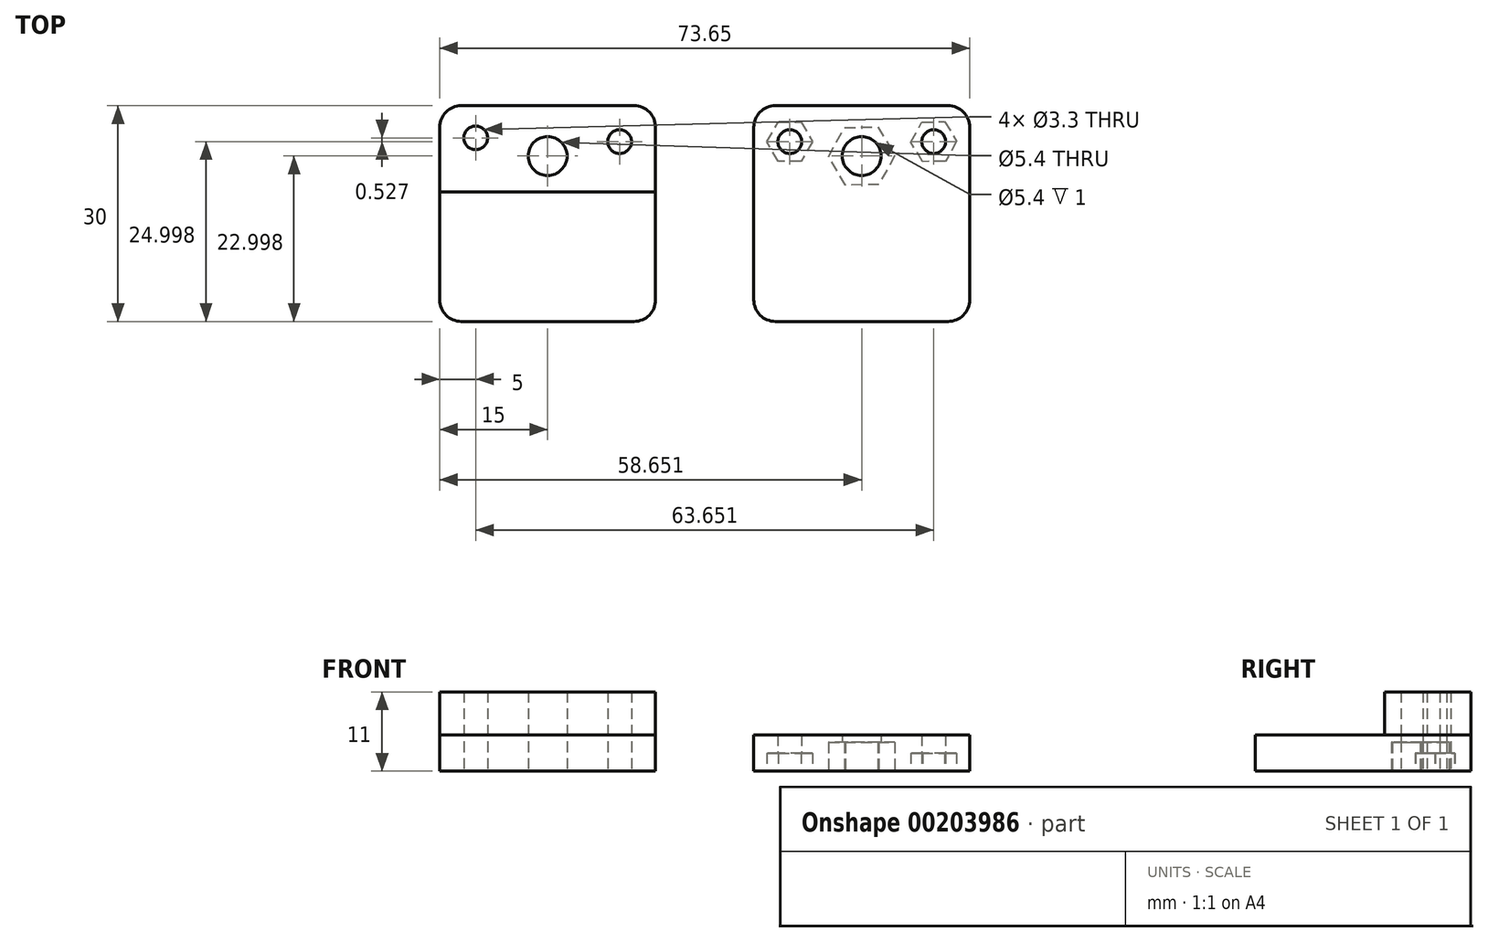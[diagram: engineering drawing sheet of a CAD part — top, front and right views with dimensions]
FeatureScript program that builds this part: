
annotation { "Feature Type Name" : "Feature", "Feature Type Description" : "" }
export const myFeature = defineFeature(function(context is Context, id is Id, definition is map)
    precondition{}
    {
        {
            var Q0;
            Q0=qCreatedBy(makeId("Top.planeOp"),FACE);
            var sketch = newSketch(context, id + "F0", { "sketchPlane" : qUnion([Q0])});
            skLineSegment(sketch, "E0.bottom", {"start": v(-35.25, 15.2) * mm, "end": v(-5.25, 15.2) * mm});
            skLineSegment(sketch, "E0.top", {"start": v(-35.25, -14.8) * mm, "end": v(-5.25, -14.8) * mm});
            skLineSegment(sketch, "E0.left", {"start": v(-35.25, 15.2) * mm, "end": v(-35.25, -14.8) * mm});
            skLineSegment(sketch, "E0.right", {"start": v(-5.25, 15.2) * mm, "end": v(-5.25, -14.8) * mm});
            skLineSegment(sketch, "E1.bottom", {"start": v(8.4, 15.2) * mm, "end": v(38.4, 15.2) * mm});
            skLineSegment(sketch, "E1.top", {"start": v(8.4, -14.8) * mm, "end": v(38.4, -14.8) * mm});
            skLineSegment(sketch, "E1.left", {"start": v(8.4, 15.2) * mm, "end": v(8.4, -14.8) * mm});
            skLineSegment(sketch, "E1.right", {"start": v(38.4, 15.2) * mm, "end": v(38.4, -14.8) * mm});
            skSolve(sketch);
        }
        {
            var Q0;
            Q0=makeQuery(id+"F0.imprint","IMPRINT",FACE,{"disambiguationData":[TD([[makeQuery(id+"F0.imprint","IMPRINT",EDGE,{"derivedFrom":sQuery(id+"F0.wireOp",EDGE,"E0.bottom")}),-1.0]])]});
            var Q1;
            Q1=makeQuery(id+"F0.imprint","IMPRINT",FACE,{"disambiguationData":[TD([[makeQuery(id+"F0.imprint","IMPRINT",EDGE,{"derivedFrom":sQuery(id+"F0.wireOp",EDGE,"E1.bottom")}),-1.0]])]});
            extrude(context, id + "F1", {"entities" : qUnion([Q0, Q1]), "depth" : 5 * mm});
        }
        {
            var Q0;
            Q0=makeQuery(id+"F1.opExtrude","CAP_FACE",FACE,{"disambiguationData":[OSD([sQuery(id+"F0.wireOp",EDGE,"E0.bottom"),sQuery(id+"F0.wireOp",EDGE,"E0.top"),sQuery(id+"F0.wireOp",EDGE,"E0.left"),sQuery(id+"F0.wireOp",EDGE,"E0.right")])],"isStart":false});
            var sketch = newSketch(context, id + "F2", { "sketchPlane" : qUnion([Q0])});
            skLineSegment(sketch, "E2.bottom", {"start": v(-35.25, 15.2) * mm, "end": v(-5.25, 15.2) * mm});
            skLineSegment(sketch, "E2.top", {"start": v(-35.25, 3.2) * mm, "end": v(-5.25, 3.2) * mm});
            skLineSegment(sketch, "E2.left", {"start": v(-35.25, 15.2) * mm, "end": v(-35.25, 3.2) * mm});
            skLineSegment(sketch, "E2.right", {"start": v(-5.25, 15.2) * mm, "end": v(-5.25, 3.2) * mm});
            skSolve(sketch);
        }
        {
            var Q0;
            Q0=makeQuery(id+"F2.imprint","IMPRINT",FACE,{"disambiguationData":[TD([[makeQuery(id+"F2.imprint","IMPRINT",EDGE,{"derivedFrom":sQuery(id+"F2.wireOp",EDGE,"E2.bottom")}),-1.0]])]});
            extrude(context, id + "F3", {"entities" : qUnion([Q0]), "operationType" : NewBodyOperationType.ADD, "depth" : 6 * mm});
        }
        {
            var Q0;
            Q0=qCreatedBy(makeId("Top.planeOp"),FACE);
            var sketch = newSketch(context, id + "F4", { "sketchPlane" : qUnion([Q0])});
            skCircle(sketch, "E3", {"center": v(23.4, 8.2) * mm, "radius": 2.7 * mm});
            skCircle(sketch, "E4", {"center": v(-20.25, 8.2) * mm, "radius": 2.7 * mm});
            skCircle(sketch, "E5", {"center": v(-30.25, 10.72) * mm, "radius": 1.65 * mm});
            skCircle(sketch, "E6", {"center": v(-10.25, 10.2) * mm, "radius": 1.65 * mm});
            skCircle(sketch, "E7", {"center": v(13.4, 10.2) * mm, "radius": 1.65 * mm});
            skCircle(sketch, "E8", {"center": v(33.4, 10.2) * mm, "radius": 1.65 * mm});
            skSolve(sketch);
        }
        {
            var Q0;
            Q0=makeQuery(id+"F4.imprint","IMPRINT",FACE,{"disambiguationData":[TD([[makeQuery(id+"F4.imprint","IMPRINT",EDGE,{"derivedFrom":sQuery(id+"F4.wireOp",EDGE,"E8")}),1.0]])]});
            var Q1;
            Q1=makeQuery(id+"F4.imprint","IMPRINT",FACE,{"disambiguationData":[TD([[makeQuery(id+"F4.imprint","IMPRINT",EDGE,{"derivedFrom":sQuery(id+"F4.wireOp",EDGE,"E3")}),1.0]])]});
            var Q2;
            Q2=makeQuery(id+"F4.imprint","IMPRINT",FACE,{"disambiguationData":[TD([[makeQuery(id+"F4.imprint","IMPRINT",EDGE,{"derivedFrom":sQuery(id+"F4.wireOp",EDGE,"E7")}),1.0]])]});
            var Q3;
            Q3=makeQuery(id+"F4.imprint","IMPRINT",FACE,{"disambiguationData":[TD([[makeQuery(id+"F4.imprint","IMPRINT",EDGE,{"derivedFrom":sQuery(id+"F4.wireOp",EDGE,"E6")}),1.0]])]});
            var Q4;
            Q4=makeQuery(id+"F4.imprint","IMPRINT",FACE,{"disambiguationData":[TD([[makeQuery(id+"F4.imprint","IMPRINT",EDGE,{"derivedFrom":sQuery(id+"F4.wireOp",EDGE,"E4")}),1.0]])]});
            var Q5;
            Q5=makeQuery(id+"F4.imprint","IMPRINT",FACE,{"disambiguationData":[TD([[makeQuery(id+"F4.imprint","IMPRINT",EDGE,{"derivedFrom":sQuery(id+"F4.wireOp",EDGE,"E5")}),1.0]])]});
            extrude(context, id + "F5", {"entities" : qUnion([Q0, Q1, Q2, Q3, Q4, Q5]), "operationType" : NewBodyOperationType.REMOVE, "endBound" : BoundingType.THROUGH_ALL, "depth" : 25 * mm});
        }
        {
            var Q0;
            Q0=qCreatedBy(makeId("Top.planeOp"),FACE);
            var sketch = newSketch(context, id + "F6", { "sketchPlane" : qUnion([Q0])});
            skCircle(sketch, "E9.cCircle", {"center": v(13.4, 10.2) * mm, "radius": 2.75 * mm, "construction": true});
            skLineSegment(sketch, "E9.0", {"start": v(16.58, 10.2) * mm, "end": v(15, 7.45) * mm});
            skLineSegment(sketch, "E9.1", {"start": v(15, 7.45) * mm, "end": v(11.82, 7.45) * mm});
            skLineSegment(sketch, "E9.2", {"start": v(11.82, 7.45) * mm, "end": v(10.23, 10.2) * mm});
            skLineSegment(sketch, "E9.3", {"start": v(10.23, 10.2) * mm, "end": v(11.81, 12.95) * mm});
            skLineSegment(sketch, "E9.4", {"start": v(11.81, 12.95) * mm, "end": v(14.99, 12.95) * mm});
            skLineSegment(sketch, "E9.5", {"start": v(14.99, 12.95) * mm, "end": v(16.58, 10.2) * mm});
            skPoint(sketch, "E9.0.midPoint", {"position": v(15.78, 8.83) * mm});
            skCircle(sketch, "E10.cCircle", {"center": v(23.4, 8.2) * mm, "radius": 4 * mm, "construction": true});
            skLineSegment(sketch, "E10.0", {"start": v(28.02, 8.28) * mm, "end": v(25.78, 4.24) * mm});
            skLineSegment(sketch, "E10.1", {"start": v(25.78, 4.24) * mm, "end": v(21.16, 4.16) * mm});
            skLineSegment(sketch, "E10.2", {"start": v(21.16, 4.16) * mm, "end": v(18.78, 8.12) * mm});
            skLineSegment(sketch, "E10.3", {"start": v(18.78, 8.12) * mm, "end": v(21.02, 12.16) * mm});
            skLineSegment(sketch, "E10.4", {"start": v(21.02, 12.16) * mm, "end": v(25.64, 12.24) * mm});
            skLineSegment(sketch, "E10.5", {"start": v(25.64, 12.24) * mm, "end": v(28.02, 8.28) * mm});
            skPoint(sketch, "E10.0.midPoint", {"position": v(26.9, 6.26) * mm});
            skCircle(sketch, "E11.cCircle", {"center": v(33.4, 10.2) * mm, "radius": 2.75 * mm, "construction": true});
            skLineSegment(sketch, "E11.0", {"start": v(36.58, 10.25) * mm, "end": v(35.04, 7.48) * mm});
            skLineSegment(sketch, "E11.1", {"start": v(35.04, 7.48) * mm, "end": v(31.86, 7.42) * mm});
            skLineSegment(sketch, "E11.2", {"start": v(31.86, 7.42) * mm, "end": v(30.23, 10.14) * mm});
            skLineSegment(sketch, "E11.3", {"start": v(30.23, 10.14) * mm, "end": v(31.76, 12.92) * mm});
            skLineSegment(sketch, "E11.4", {"start": v(31.76, 12.92) * mm, "end": v(34.94, 12.98) * mm});
            skLineSegment(sketch, "E11.5", {"start": v(34.94, 12.98) * mm, "end": v(36.58, 10.25) * mm});
            skPoint(sketch, "E11.0.midPoint", {"position": v(35.8, 8.87) * mm});
            skSolve(sketch);
        }
        {
            var Q0;
            Q0=makeQuery(id+"F6.imprint","IMPRINT",FACE,{"disambiguationData":[TD([[makeQuery(id+"F6.imprint","IMPRINT",EDGE,{"derivedFrom":sQuery(id+"F6.wireOp",EDGE,"E9.0")}),-1.0]])]});
            var Q1;
            Q1=makeQuery(id+"F6.imprint","IMPRINT",FACE,{"disambiguationData":[TD([[makeQuery(id+"F6.imprint","IMPRINT",EDGE,{"derivedFrom":sQuery(id+"F6.wireOp",EDGE,"E10.0")}),-1.0]])]});
            var Q2;
            Q2=makeQuery(id+"F6.imprint","IMPRINT",FACE,{"disambiguationData":[TD([[makeQuery(id+"F6.imprint","IMPRINT",EDGE,{"derivedFrom":sQuery(id+"F6.wireOp",EDGE,"E11.0")}),-1.0]])]});
            extrude(context, id + "F7", {"entities" : qUnion([Q0, Q1, Q2]), "operationType" : NewBodyOperationType.REMOVE, "depth" : 2.5 * mm});
        }
        {
            var Q0;
            Q0=makeQuery(id+"F7.boolean.opBoolean","COPY",FACE,{"derivedFrom":makeQuery(id+"F7.opExtrude","CAP_FACE",FACE,{"disambiguationData":[OSD([sQuery(id+"F6.wireOp",EDGE,"E10.0"),sQuery(id+"F6.wireOp",EDGE,"E10.1"),sQuery(id+"F6.wireOp",EDGE,"E10.2"),sQuery(id+"F6.wireOp",EDGE,"E10.3"),sQuery(id+"F6.wireOp",EDGE,"E10.4"),sQuery(id+"F6.wireOp",EDGE,"E10.5")])],"isStart":false})});
            extrude(context, id + "F8", {"entities" : qUnion([Q0]), "operationType" : NewBodyOperationType.REMOVE, "oppositeDirection" : true, "depth" : 1.5 * mm});
        }
        {
            var Q0;
            Q0=makeQuery(id+"F1.opExtrude","SWEPT_EDGE",EDGE,{"disambiguationData":[OSD([sQuery(id+"F0.wireOp",EDGE,"E1.top"),sQuery(id+"F0.wireOp",EDGE,"E1.right")])]});
            var Q1;
            Q1=makeQuery(id+"F1.opExtrude","SWEPT_EDGE",EDGE,{"disambiguationData":[OSD([sQuery(id+"F0.wireOp",EDGE,"E1.bottom"),sQuery(id+"F0.wireOp",EDGE,"E1.right")])]});
            var Q2;
            Q2=makeQuery(id+"F1.opExtrude","SWEPT_EDGE",EDGE,{"disambiguationData":[OSD([sQuery(id+"F0.wireOp",EDGE,"E1.top"),sQuery(id+"F0.wireOp",EDGE,"E1.left")])]});
            var Q3;
            Q3=makeQuery(id+"F1.opExtrude","SWEPT_EDGE",EDGE,{"disambiguationData":[OSD([sQuery(id+"F0.wireOp",EDGE,"E1.bottom"),sQuery(id+"F0.wireOp",EDGE,"E1.left")])]});
            var Q4;
            Q4=makeQuery(id+"F1.opExtrude","SWEPT_EDGE",EDGE,{"disambiguationData":[OSD([sQuery(id+"F0.wireOp",EDGE,"E0.top"),sQuery(id+"F0.wireOp",EDGE,"E0.right")])]});
            var Q5;
            Q5=makeQuery(id+"F1.opExtrude","SWEPT_EDGE",EDGE,{"disambiguationData":[OSD([sQuery(id+"F0.wireOp",EDGE,"E0.top"),sQuery(id+"F0.wireOp",EDGE,"E0.left")])]});
            var Q6;
            Q6=makeQuery(id+"F3.boolean.opBoolean","MERGE",EDGE,{"derivedFrom":[makeQuery(id+"F1.opExtrude","SWEPT_EDGE",EDGE,{"disambiguationData":[OSD([sQuery(id+"F0.wireOp",EDGE,"E0.bottom"),sQuery(id+"F0.wireOp",EDGE,"E0.left")])]}),makeQuery(id+"F3.opExtrude","SWEPT_EDGE",EDGE,{"disambiguationData":[OSD([sQuery(id+"F2.wireOp",EDGE,"E2.bottom"),sQuery(id+"F2.wireOp",EDGE,"E2.left")])]})]});
            var Q7;
            Q7=makeQuery(id+"F3.boolean.opBoolean","MERGE",EDGE,{"derivedFrom":[makeQuery(id+"F1.opExtrude","SWEPT_EDGE",EDGE,{"disambiguationData":[OSD([sQuery(id+"F0.wireOp",EDGE,"E0.bottom"),sQuery(id+"F0.wireOp",EDGE,"E0.right")])]}),makeQuery(id+"F3.opExtrude","SWEPT_EDGE",EDGE,{"disambiguationData":[OSD([sQuery(id+"F2.wireOp",EDGE,"E2.bottom"),sQuery(id+"F2.wireOp",EDGE,"E2.right")])]})]});
            fillet(context, id + "F9", {"entities" : qUnion([Q0, Q1, Q2, Q3, Q4, Q5, Q6, Q7]), "radius" : 3 * mm, "tangentPropagation" : true, "allowEdgeOverflow" : false});
        }
    });
